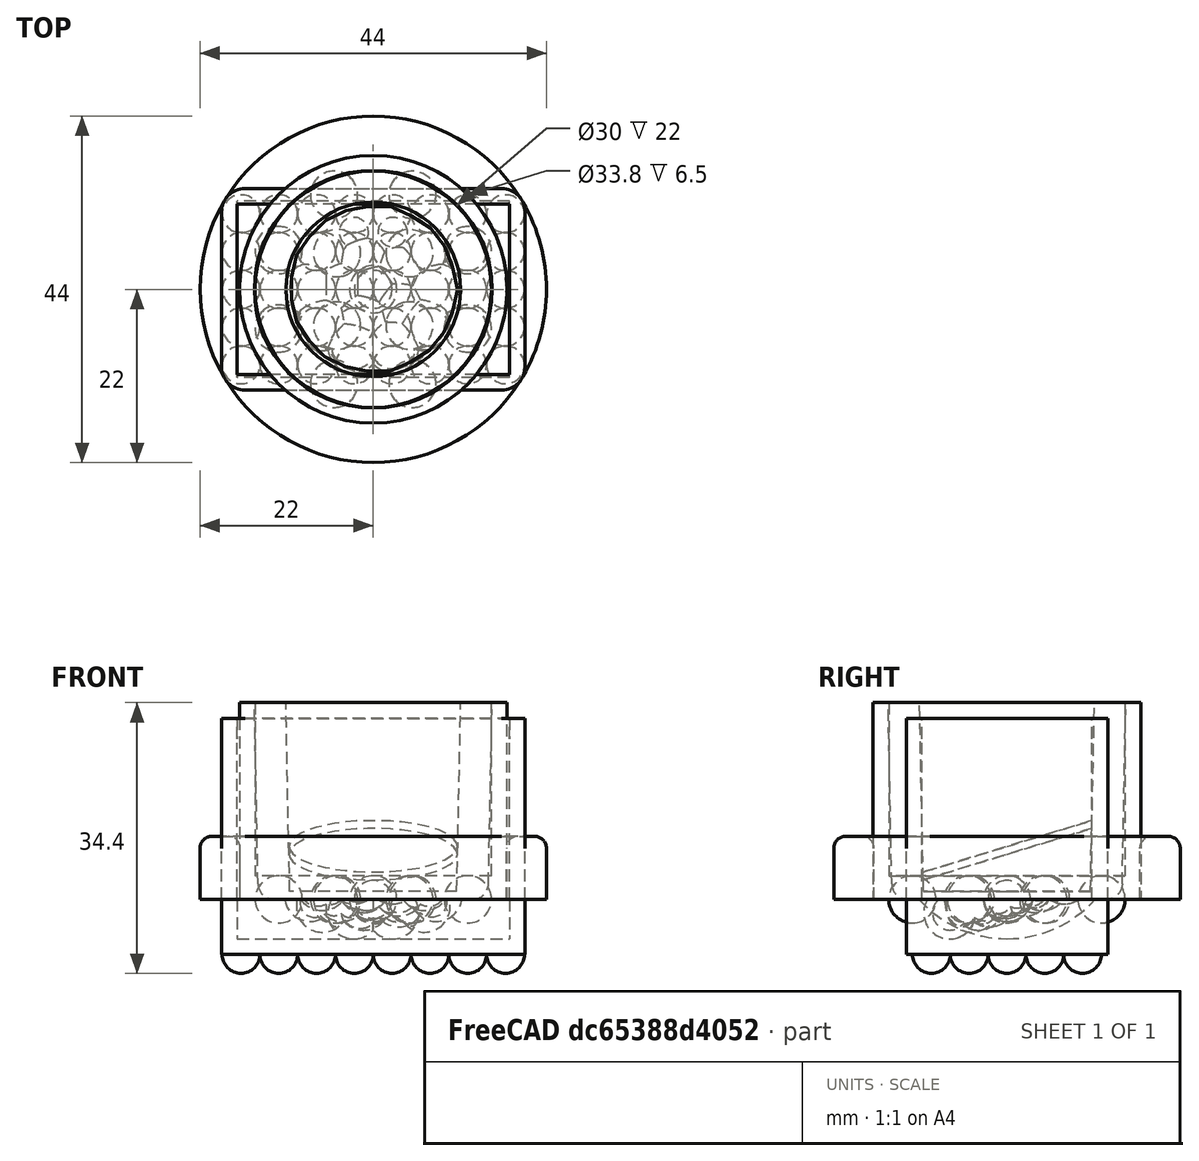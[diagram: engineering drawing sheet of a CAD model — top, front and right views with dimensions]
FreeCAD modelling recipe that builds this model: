
FCSTD DOCUMENT  (FreeCAD 1.0R39109 (Git))
Label: chair_leg_pad
License: All rights reserved
LicenseURL: http://en.wikipedia.org/wiki/All_rights_reserved
objects: Part::FeaturePython×7, Part::Cut×5, Part::MultiFuse×4, App::Part×4, Part::Cylinder×3, Part::Sphere×3, Part::Fillet×3, Part::Box×3, Part::Cone×2, Part::Plane×2, App::DocumentObjectGroup×1
note: 30 computed .brp shape members not serialized (recipe doc carries the construction recipe); baked Part::Feature solids carry a one-line shape summary decoded from their .brp

FEATURE [Part::Cylinder] Cylinder  label="inner cylinder"
  Angle = 360
  AttacherType = Attacher::AttachEngine3D
  FirstAngle = 0
  Height = 25
  Placement = pos=(0,0,3) rot=(0,0,1;0rad)
  Radius = 15
  SecondAngle = 0
FEATURE [Part::Cylinder] Cylinder001  label="outer cylinder"
  Angle = 360
  AttacherType = Attacher::AttachEngine3D
  FirstAngle = 0
  Height = 25
  Radius = 17
  SecondAngle = 0
FEATURE [Part::Sphere] Sphere
  Angle1 = -90
  Angle2 = 90
  Angle3 = 360
  AttacherType = Attacher::AttachEngine3D
  Radius = 3
FEATURE [Part::FeaturePython] Array  # Draft array (typed FeaturePython)
  AlwaysSyncPlacement = false
  Angle = 360
  ArrayType = 2
  Axis = (0,0,1)
  AxisReference = -> Sphere
  Base = -> Sphere
  Center = (12.35,59.91,0)
  Count = 25
  ExpandArray = false
  Fuse = false
  IntervalAxis = (0,0,0)
  IntervalX = (50,0,0)
  IntervalY = (0,50,0)
  IntervalZ = (0,0,50)
  NumberCircles = 3
  NumberPolar = 5
  NumberX = 2
  NumberY = 2
  NumberZ = 1
  PlacementList = 25 placements: [(0,0,0),(-6.5,0,0),(-4.59619,-4.59619,0),(-1.44329e-15,-6.5,0),(4.59619,-4.59619,0),(6.5,-7.9602e-16,0),(4.59619,4.59619,0),(1.44329e-15,6.5,0),(-4.59619,4.59619,0),(-13,0,0),(-12.0104,-4.97488,0),(-9.19239,-9.19239,0),(-4.97488,-12.0104,0),(-2.88658e-15,-13,0),(4.97488,-12.0104,0),(9.19239,-9.19239,0),(12.0104,-4.97488,0),(13,-1.59204e-15,0),(12.0104,4.97488,0),(9.19239,9.19239,0),+5 more]
  RadialDistance = 6.5
  ScaleList = (25) [(1,1,1),(1,1,1),(1,1,1),(1,1,1),(1,1,1),(1,1,1),(1,1,1),(1,1,1),(1,1,1),(1,1,1),(1,1,1),(1,1,1),(1,1,1),(1,1,1),(1,1,1),(1,1,1),(1,1,1),(1,1,1),+7 more]
  Symmetry = 1
  TangentialDistance = 5
FEATURE [Part::MultiFuse] Fusion  label="fusion"
  Shapes = -> [Cylinder001,Array]
FEATURE [Part::Cut] Cut  label="chair leg pad"
  Base = -> Fusion
  Tool = -> Cylinder
FEATURE [Part::Sphere] Sphere001
  Angle1 = -90
  Angle2 = 90
  Angle3 = 360
  AttacherType = Attacher::AttachEngine3D
  Radius = 3.3
FEATURE [Part::FeaturePython] Array001  # Draft array (typed FeaturePython)
  AlwaysSyncPlacement = false
  Angle = 360
  ArrayType = 2
  Axis = (0,0,1)
  AxisReference = -> Sphere001
  Base = -> Sphere001
  Center = (12.35,59.91,0)
  Count = 16
  ExpandArray = false
  Fuse = true
  IntervalAxis = (0,0,0)
  IntervalX = (50,0,0)
  IntervalY = (0,50,0)
  IntervalZ = (0,0,50)
  NumberCircles = 3
  NumberPolar = 5
  NumberX = 2
  NumberY = 2
  NumberZ = 1
  Placement = pos=(0,0,0.5) rot=(1,0,0;0.296706rad)
  PlacementList = 16 placements: [(0,0,0),(-4,0,0),(-1.23607,-3.80423,0),(3.23607,-2.35114,0),(3.23607,2.35114,0),(-1.23607,3.80423,0),(-8,0,0),(-6.47214,-4.70228,0),(-2.47214,-7.60845,0),(2.47214,-7.60845,0),(6.47214,-4.70228,0),(8,-9.79717e-16,0),(6.47214,4.70228,0),(2.47214,7.60845,0),(-2.47214,7.60845,0),(-6.47214,4.70228,0)]
  RadialDistance = 4
  ScaleList = (16) [(1,1,1),(1,1,1),(1,1,1),(1,1,1),(1,1,1),(1,1,1),(1,1,1),(1,1,1),(1,1,1),(1,1,1),(1,1,1),(1,1,1),(1,1,1),(1,1,1),(1,1,1),(1,1,1)]
  Symmetry = 1
  TangentialDistance = 5
FEATURE [Part::Cone] Cone  label="inner cone"
  Angle = 360
  AttacherType = Attacher::AttachEngine3D
  Height = 25
  Placement = pos=(0,0,1) rot=(0,0,1;0rad)
  Radius1 = 10.6
  Radius2 = 11.1
FEATURE [Part::Cone] Cone001  label="outer cone"
  Angle = 360
  AttacherType = Attacher::AttachEngine3D
  Height = 25
  Radius1 = 14.6
  Radius2 = 15.1
  expr: Height = <<inner cone>>.Height
  expr: Radius1 = <<inner cone>>.Radius1 + 4 mm
  expr: Radius2 = <<inner cone>>.Radius2 + 4 mm
FEATURE [Part::Plane] Plane  label="bottom cut plane"
  AttacherType = Attacher::AttachEngine3D
  Length = 50
  Placement = pos=(-24,-22,0) rot=(1,0,0;0.296706rad)
  Width = 50
FEATURE [Part::FeaturePython] Slice  # WARN: FeaturePython — macro-defined, semantics opaque (R4)
  Base = -> Cone
  Mode = 1
  Tolerance = 0
  Tools = -> [Plane]
FEATURE [Part::Plane] Plane001  label="test size cut plane"
  AttacherType = Attacher::AttachEngine3D
  Length = 100
  Placement = pos=(-35,-50,17) rot=(0,0,1;0rad)
  Width = 100
FEATURE [Part::Fillet] Fillet  label="outer cone fillet"
  Base = -> Cone001
  EdgeLinks = -> Cone001 [Edge3]
  Edges = 1 edges r=2: [Edge3]
FEATURE [Part::MultiFuse] Fusion001  label="fusion001"
  Shapes = -> [Array001,Fillet]
FEATURE [App::Part] Part  label="chair leg pad part"
  Group = -> [Cut]
  Origin = -> Origin
FEATURE [Part::FeaturePython] Slice_child0  label="Slice.0"  # WARN: FeaturePython — macro-defined, semantics opaque (R4)
  Base = -> Slice
  FilterType = 1
  Invert = false
  OverrideMaxVal = 0
  Placement = pos=(0,0,-1) rot=(0,0,1;0rad)
  WindowFrom = 80
  WindowTo = 100
  items = 0
FEATURE [Part::Cut] Cut001  label="chair cone leg pad"
  Base = -> Fusion001
  Tool = -> Slice_child0
FEATURE [App::Part] Part001  label="chair cone leg pad part"
  Group = -> [Cut001]
  Origin = -> Origin001
FEATURE [Part::FeaturePython] Slice_child1  label="Slice.1"  # WARN: FeaturePython — macro-defined, semantics opaque (R4)
  Base = -> Slice
  FilterType = 1
  Invert = false
  OverrideMaxVal = 0
  WindowFrom = 80
  WindowTo = 100
  items = 1
FEATURE [App::DocumentObjectGroup] GrExplode_Slice  label="chair cone leg pad Exploded Slice"
  Group = -> [Slice_child0,Slice_child1]
FEATURE [Part::Box] Box  label="internal cube"
  AttacherType = Attacher::AttachEngine3D
  Height = 100
  Length = 34.6
  Placement = pos=(-17.3,-10.8,0) rot=(0,0,1;0rad)
  Width = 21.6
  expr: .Placement.Base.x = -Length / 2
  expr: .Placement.Base.y = -Width / 2
FEATURE [Part::Box] Box001  label="external cube"
  AttacherType = Attacher::AttachEngine3D
  Height = 30
  Length = 38.6
  Placement = pos=(-19.3,-12.8,-7) rot=(0,0,1;0rad)
  Width = 25.6
  expr: .Placement.Base.x = -Length / 2
  expr: .Placement.Base.y = -Width / 2
  expr: .Placement.Base.z = <<internal cube>>.Placement.Base.z - 7 mm
  expr: Length = <<internal cube>>.Length + 4 mm
  expr: Width = <<internal cube>>.Width + 4 mm
FEATURE [Part::Cylinder] Cylinder002  label="extract cylinder"
  Angle = 360
  AttacherType = Attacher::AttachEngine3D
  FirstAngle = 0
  Height = 34.6
  Placement = pos=(-17.3,0,10) rot=(0,1,0;1.5708rad)
  Radius = 15
  SecondAngle = 0
  expr: .Placement.Base.x = -Height / 2
  expr: Height = <<internal cube>>.Length
FEATURE [Part::Box] Box002  label="big removal cube"
  AttacherType = Attacher::AttachEngine3D
  Height = 100
  Length = 34.6
  Placement = pos=(-17.3,-35.8,0) rot=(0,0,1;0rad)
  Width = 71.6
  expr: .Placement.Base.x = -Length / 2
  expr: .Placement.Base.y = -Width / 2
  expr: Height = <<internal cube>>.Height
  expr: Length = <<internal cube>>.Length
  expr: Width = <<internal cube>>.Width + 50 mm
FEATURE [Part::Cut] Cut002  label="cylinder cut"
  Base = -> Box002
  Tool = -> Box
FEATURE [Part::Cut] Cut003  label="rounded extract cut"
  Base = -> Cylinder002
  Tool = -> Cut002
FEATURE [Part::MultiFuse] Fusion002  label="extract fusion"
  Shapes = -> [Cut003,Box]
FEATURE [Part::Fillet] Fillet001  label="external fillet"
  Base = -> Box001
  EdgeLinks = -> Box001 [Edge1,Edge3,Edge5,Edge7]
  Edges = 4 edges r=3: [Edge1,Edge3,Edge5,Edge7]
FEATURE [Part::Sphere] Sphere002
  Angle1 = -90
  Angle2 = 90
  Angle3 = 360
  AttacherType = Attacher::AttachEngine3D
  Radius = 2.4
FEATURE [Part::FeaturePython] Array002  label="rectangular sphere array"  # Draft array (typed FeaturePython)
  AlwaysSyncPlacement = false
  Angle = 360
  ArrayType = 0
  Axis = (0,0,1)
  Base = -> Sphere002
  Center = (0,0,0)
  Count = 40
  ExpandArray = false
  Fuse = false
  IntervalAxis = (0,0,0)
  IntervalX = (4.8,0,0)
  IntervalY = (0,4.8,0)
  IntervalZ = (0,0,100)
  NumberCircles = 3
  NumberPolar = 5
  NumberX = 8
  NumberY = 5
  NumberZ = 1
  Placement = pos=(-16.8,-9.6,-7) rot=(0,0,1;0rad)
  PlacementList = 40 placements: [(0,0,0),(0,4.8,0),(0,9.6,0),(0,14.4,0),(0,19.2,0),(4.8,0,0),(4.8,4.8,0),(4.8,9.6,0),(4.8,14.4,0),(4.8,19.2,0),(9.6,0,0),(9.6,4.8,0),(9.6,9.6,0),(9.6,14.4,0),(9.6,19.2,0),(14.4,0,0),(14.4,4.8,0),(14.4,9.6,0),(14.4,14.4,0),(14.4,19.2,0),(19.2,0,0),(19.2,4.8,0),(19.2,9.6,0),(19.2,14.4,0),(19.2,19.2,0),(24,0,0),(24,4.8,0),(24,9.6,0),(24,14.4,0),(24,19.2,0),(28.8,0,0),(28.8,4.8,0),(28.8,9.6,0),+7 more]
  RadialDistance = 50
  ScaleList = (40) [(1,1,1),(1,1,1),(1,1,1),(1,1,1),(1,1,1),(1,1,1),(1,1,1),(1,1,1),(1,1,1),(1,1,1),(1,1,1),(1,1,1),(1,1,1),(1,1,1),(1,1,1),(1,1,1),(1,1,1),(1,1,1),+22 more]
  Symmetry = 1
  TangentialDistance = 25
  expr: .IntervalX.x = <<Sphere002>>.Radius * 2
  expr: .IntervalY.y = <<Sphere002>>.Radius * 2
  expr: .Placement.Base.z = <<external cube>>.Placement.Base.z
FEATURE [Part::MultiFuse] Fusion003  label="rectangular leg pad fusion"
  Shapes = -> [Array002,Fillet001]
FEATURE [Part::Cut] Cut004  label="rectangular leg pad cut"
  Base = -> Fusion003
  Tool = -> Fusion002
FEATURE [App::Part] Part002  label="rectangular leg pad part"
  Group = -> [Cut004]
  Origin = -> Origin002
FEATURE [Part::FeaturePython] Tube  # WARN: FeaturePython — macro-defined, semantics opaque (R4)
  AttacherType = Attacher::AttachEngine3D
  Height = 8
  InnerRadius = 16.9
  OuterRadius = 22
FEATURE [Part::Fillet] Fillet002  label="leg tube fillet"
  Base = -> Tube
  EdgeLinks = -> Tube [Edge1,Edge4]
  Edges = 2 edges r=1.5: [Edge1,Edge4]
FEATURE [App::Part] Part003  label="anycubix max4pro leg"
  Group = -> [Fillet002]
  Origin = -> Origin003
